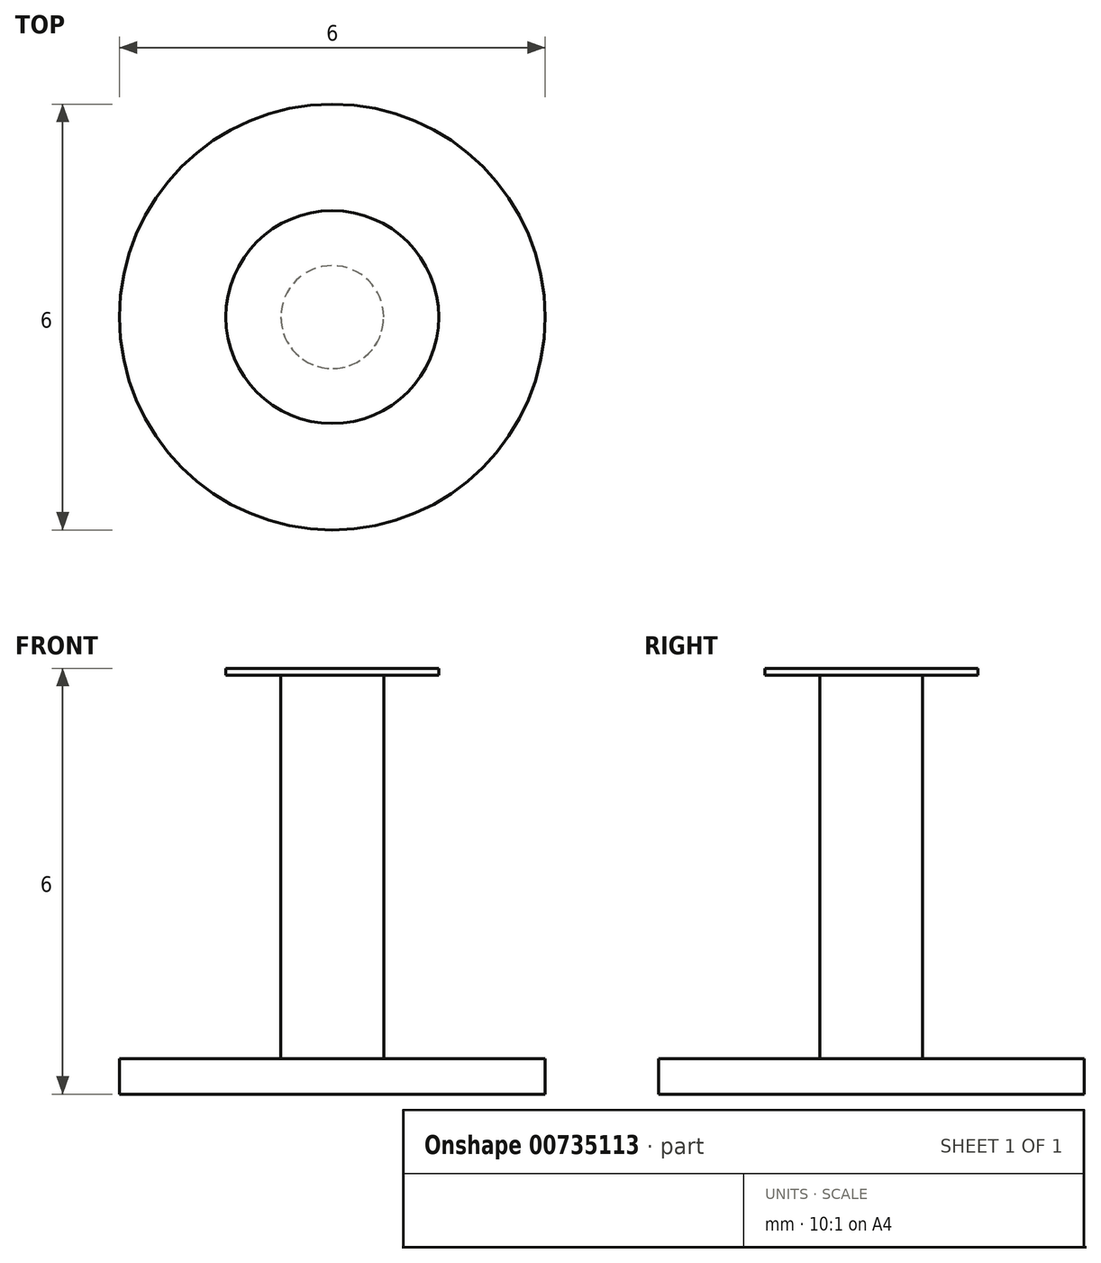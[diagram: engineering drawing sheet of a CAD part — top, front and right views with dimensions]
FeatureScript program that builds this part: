
annotation { "Feature Type Name" : "Feature", "Feature Type Description" : "" }
export const myFeature = defineFeature(function(context is Context, id is Id, definition is map)
    precondition{}
    {
        {
            var Q0;
            Q0=qCreatedBy(makeId("Top.planeOp"),FACE);
            var sketch = newSketch(context, id + "F0", { "sketchPlane" : qUnion([Q0])});
            skCircle(sketch, "E0", {"center": v(0, 0) * mm, "radius": 0.73 * mm});
            skSolve(sketch);
        }
        {
            var Q0;
            Q0 = qSketchRegion(id + "F0", true);
            extrude(context, id + "F1", {"entities" : qUnion([Q0]), "depth" : 6 * mm, "offsetDistance" : 25 * mm});
        }
        {
            var Q0;
            Q0=makeQuery(id+"F1.opExtrude","CAP_FACE",FACE,{"disambiguationData":[OSD([sQuery(id+"F0.wireOp",EDGE,"E0")])],"isStart":false});
            var sketch = newSketch(context, id + "F2", { "sketchPlane" : qUnion([Q0])});
            skCircle(sketch, "E1", {"center": v(0, 0) * mm, "radius": 1.5 * mm});
            skSolve(sketch);
        }
        {
            var Q0;
            Q0 = qSketchRegion(id + "F2", true);
            extrude(context, id + "F3", {"entities" : qUnion([Q0]), "operationType" : NewBodyOperationType.ADD, "oppositeDirection" : true, "depth" : 0.1 * mm, "offsetDistance" : 25 * mm});
        }
        {
            var Q0;
            Q0=makeQuery(id+"F1.opExtrude","CAP_FACE",FACE,{"disambiguationData":[OSD([sQuery(id+"F0.wireOp",EDGE,"E0")])],"isStart":true});
            var sketch = newSketch(context, id + "F4", { "sketchPlane" : qUnion([Q0])});
            skCircle(sketch, "E2", {"center": v(0, 0) * mm, "radius": 3 * mm});
            skSolve(sketch);
        }
        {
            var Q0;
            Q0 = qSketchRegion(id + "F4", true);
            extrude(context, id + "F5", {"entities" : qUnion([Q0]), "operationType" : NewBodyOperationType.ADD, "oppositeDirection" : true, "depth" : 0.5 * mm, "offsetDistance" : 25 * mm});
        }
    });
